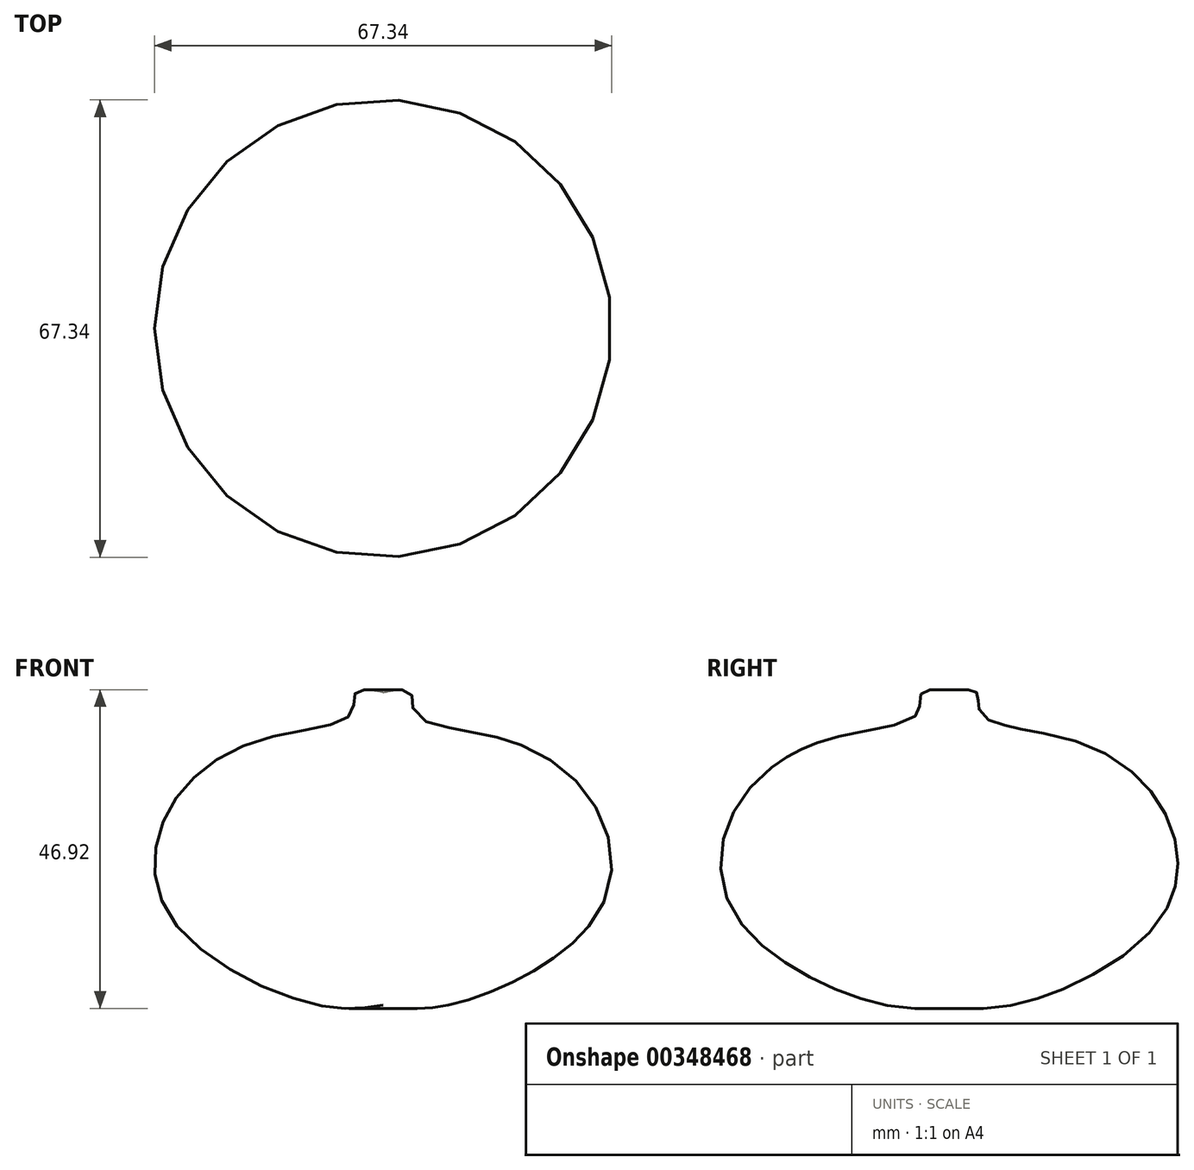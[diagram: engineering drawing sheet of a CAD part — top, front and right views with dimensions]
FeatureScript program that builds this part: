
annotation { "Feature Type Name" : "Feature", "Feature Type Description" : "" }
export const myFeature = defineFeature(function(context is Context, id is Id, definition is map)
    precondition{}
    {
        {
            var Q0;
            Q0=qCreatedBy(makeId("Front.planeOp"),FACE);
            var sketch = newSketch(context, id + "F0", { "sketchPlane" : qUnion([Q0])});
            skFitSpline(sketch, "E0", {"points": [v(0, 46) * mm, v(-4.05, 46) * mm, v(-4.68, 42.88) * mm, v(-18.71, 38.83) * mm, v(-32.12, 27.6) * mm, v(-30.88, 12.32) * mm, v(-9.67, 0) * mm, v(0, 0) * mm], "startDerivative": vector(-62.56, 12.65) * mm, "endDerivative": vector(63.27, 10.18) * mm});
            skLineSegment(sketch, "E1", {"start": v(0, 46) * mm, "end": v(0, 0) * mm, "construction": true});
            skSolve(sketch);
        }
        {
            var Q0;
            Q0 = qSketchRegion(id + "F0", true);
            var Q1;
            Q1 = qConstructionFilter(qBodyType(qCreatedBy(id + "F0" ,EDGE), BodyType.WIRE), ConstructionObject.NO);
            var Q2;
            Q2=sQuery(id+"F0.wireOp",EDGE,"E1");
            revolve(context, id + "F1", {"bodyType" : ToolBodyType.SURFACE, "entities" : qUnion([Q0]), "surfaceEntities" : qUnion([Q1]), "axis" : qUnion([Q2]), "revolveType" : RevolveType.FULL});
        }
    });
